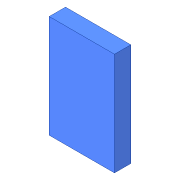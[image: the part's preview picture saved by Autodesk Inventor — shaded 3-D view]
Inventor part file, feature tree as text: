
AUTODESK INVENTOR PART (.ipt)
format: ipt  version: 2018.3 (Build 223284000, 284)  size: 79,872 bytes
history: native  units: in
note: dims shown in document units (in); Inventor stores cm internally (conversion verified against a paired STEP export)
features: extrude x1, sketch x1
ambient origin geometry x8: Origin, YZ Plane, XZ Plane, XY Plane, X Axis, Y Axis, Z Axis, Center Point
bodies: Solid1 (feature_tree)
feature tree (2):
  extrude  "Extrusion1"  Depth=1.26in
  sketch  "Sketch1"  dims[d0=0.8in d1=1.26in d2=0.2in d3=0.0in]
